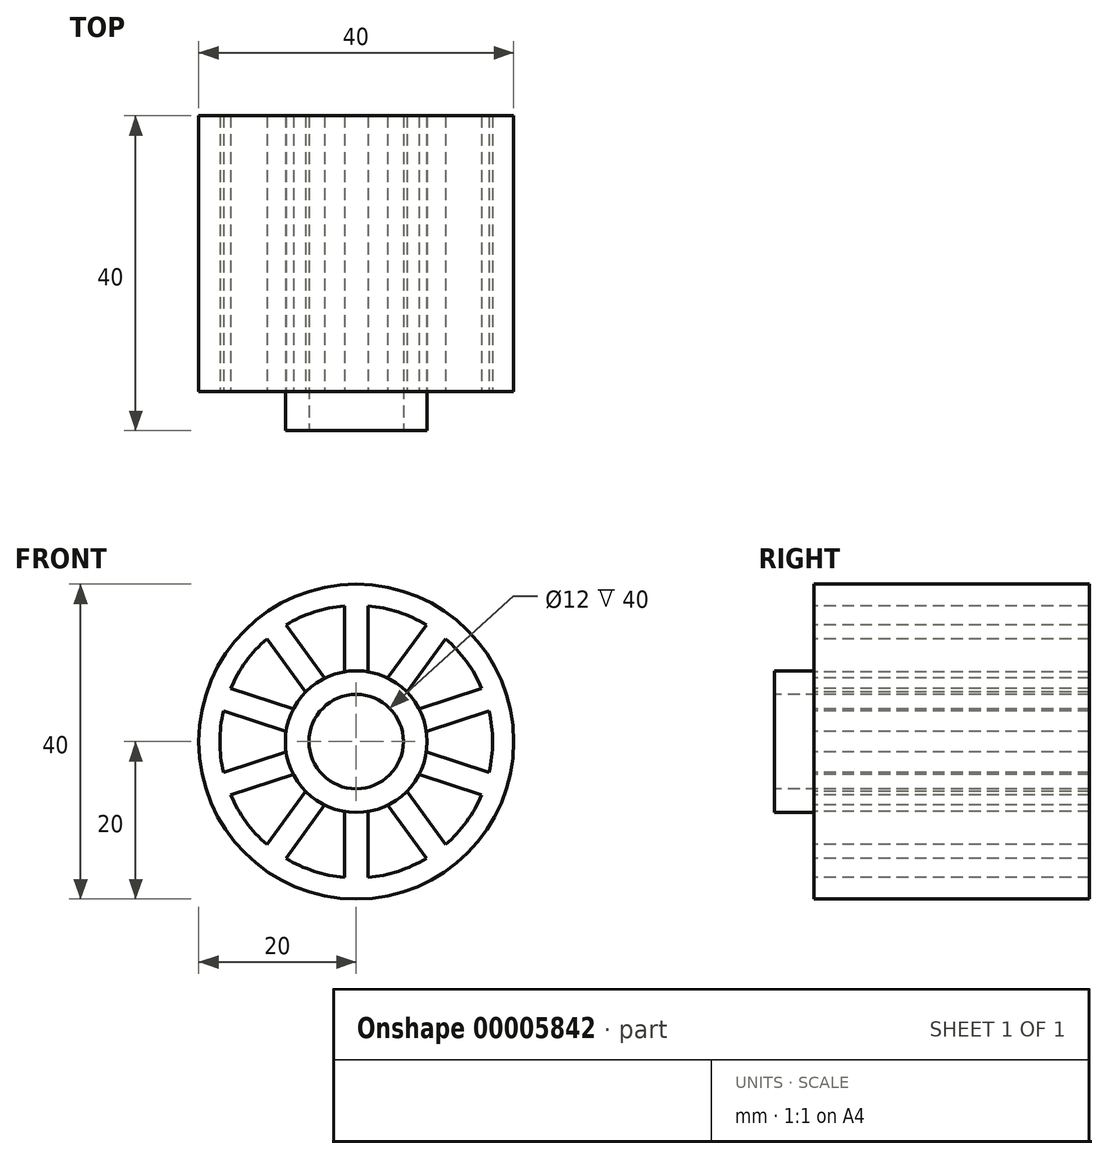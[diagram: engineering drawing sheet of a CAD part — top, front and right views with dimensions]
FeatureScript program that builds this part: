
annotation { "Feature Type Name" : "Feature", "Feature Type Description" : "" }
export const myFeature = defineFeature(function(context is Context, id is Id, definition is map)
    precondition{}
    {
        {
            var Q0;
            Q0=qCreatedBy(makeId("Front.planeOp"),FACE);
            var sketch = newSketch(context, id + "F0", { "sketchPlane" : qUnion([Q0])});
            skPoint(sketch, "E0.rect.middle", {"position": v(0, 0) * mm});
            skLineSegment(sketch, "E1.rect.left", {"start": v(1.5, 17.25) * mm, "end": v(1.5, 8.87) * mm});
            skLineSegment(sketch, "E1.rect.right", {"start": v(-1.5, 17.25) * mm, "end": v(-1.5, 8.87) * mm});
            skLineSegment(sketch, "E2.1.0", {"start": v(-16.87, 3.9) * mm, "end": v(-8.9, 1.32) * mm});
            skLineSegment(sketch, "E2.1.3", {"start": v(-15.94, 6.76) * mm, "end": v(-7.98, 4.17) * mm});
            skLineSegment(sketch, "E2.2.0", {"start": v(-8.92, -14.83) * mm, "end": v(-4, -8.06) * mm});
            skLineSegment(sketch, "E2.2.3", {"start": v(-11.35, -13.07) * mm, "end": v(-6.43, -6.3) * mm});
            skLineSegment(sketch, "E2.3.0", {"start": v(11.35, -13.07) * mm, "end": v(6.43, -6.3) * mm});
            skLineSegment(sketch, "E2.3.3", {"start": v(8.92, -14.83) * mm, "end": v(4, -8.06) * mm});
            skLineSegment(sketch, "E2.4.0", {"start": v(15.94, 6.76) * mm, "end": v(7.98, 4.17) * mm});
            skLineSegment(sketch, "E2.4.3", {"start": v(16.87, 3.9) * mm, "end": v(8.9, 1.32) * mm});
            skCircle(sketch, "E3", {"center": v(0, 0) * mm, "radius": 20 * mm});
            skArc(sketch, "E4", {"start": v(8.92, 14.83) * mm, "mid": v(5.35, 16.46) * mm, "end": v(1.5, 17.25) * mm});
            skArc(sketch, "E5", {"start": v(-7.98, -4.17) * mm, "mid": v(-7.28, -5.3) * mm, "end": v(-6.43, -6.3) * mm});
            skCircle(sketch, "E6", {"center": v(0, 0) * mm, "radius": 6 * mm});
            skPoint(sketch, "E7.orphan", {"position": v(-12.09, 14.09) * mm});
            skPoint(sketch, "E8.orphan", {"position": v(-9.66, 15.85) * mm});
            skPoint(sketch, "E9.orphan", {"position": v(12.09, 14.09) * mm});
            skArc(sketch, "E10.trimOffspring", {"start": v(15.94, 6.76) * mm, "mid": v(14, 10.18) * mm, "end": v(11.35, 13.07) * mm});
            skPoint(sketch, "E11.orphan", {"position": v(18.06, 4.3) * mm});
            skArc(sketch, "E12.trimOffspring", {"start": v(-1.5, 17.25) * mm, "mid": v(-5.35, 16.46) * mm, "end": v(-8.92, 14.83) * mm});
            skPoint(sketch, "E1.rect.bottom.end.orphan", {"position": v(-1.5, 18.5) * mm});
            skPoint(sketch, "E1.rect.bottom.start.orphan", {"position": v(1.5, 18.5) * mm});
            skLineSegment(sketch, "E13.trimOffspring", {"start": v(-4, 8.06) * mm, "end": v(-8.92, 14.83) * mm});
            skLineSegment(sketch, "E14.trimOffspring", {"start": v(-6.43, 6.3) * mm, "end": v(-11.35, 13.07) * mm});
            skArc(sketch, "E15.trimOffspring", {"start": v(-11.35, 13.07) * mm, "mid": v(-14, 10.18) * mm, "end": v(-15.94, 6.76) * mm});
            skPoint(sketch, "E16.orphan", {"position": v(-18.06, 4.3) * mm});
            skPoint(sketch, "E17.orphan", {"position": v(-17.13, 7.14) * mm});
            skArc(sketch, "E18.trimOffspring", {"start": v(-16.87, 3.9) * mm, "mid": v(-17.31, 0) * mm, "end": v(-16.87, -3.9) * mm});
            skPoint(sketch, "E19.orphan", {"position": v(-17.13, -7.14) * mm});
            skArc(sketch, "E20.trimOffspring", {"start": v(-15.94, -6.76) * mm, "mid": v(-14, -10.18) * mm, "end": v(-11.35, -13.07) * mm});
            skLineSegment(sketch, "E21.trimOffspring", {"start": v(4, 8.06) * mm, "end": v(8.92, 14.83) * mm});
            skLineSegment(sketch, "E22.trimOffspring", {"start": v(6.43, 6.3) * mm, "end": v(11.35, 13.07) * mm});
            skLineSegment(sketch, "E23.trimOffspring", {"start": v(-8.9, -1.32) * mm, "end": v(-16.87, -3.9) * mm});
            skArc(sketch, "E24.trimOffspring", {"start": v(-8.9, 1.32) * mm, "mid": v(-9, 0) * mm, "end": v(-8.9, -1.32) * mm});
            skArc(sketch, "E25.trimOffspring", {"start": v(-6.43, 6.3) * mm, "mid": v(-7.28, 5.3) * mm, "end": v(-7.98, 4.17) * mm});
            skArc(sketch, "E26.trimOffspring", {"start": v(-1.5, 8.87) * mm, "mid": v(-2.78, 8.56) * mm, "end": v(-4, 8.06) * mm});
            skArc(sketch, "E27.trimOffspring", {"start": v(4, 8.06) * mm, "mid": v(2.78, 8.56) * mm, "end": v(1.5, 8.87) * mm});
            skArc(sketch, "E28.trimOffspring", {"start": v(7.98, 4.17) * mm, "mid": v(7.28, 5.3) * mm, "end": v(6.43, 6.3) * mm});
            skArc(sketch, "E29.trimOffspring", {"start": v(8.9, -1.32) * mm, "mid": v(9, 0) * mm, "end": v(8.9, 1.32) * mm});
            skLineSegment(sketch, "E30.trimOffspring", {"start": v(8.9, -1.32) * mm, "end": v(16.87, -3.9) * mm});
            skLineSegment(sketch, "E31.trimOffspring", {"start": v(7.98, -4.17) * mm, "end": v(15.94, -6.76) * mm});
            skLineSegment(sketch, "E32.trimOffspring", {"start": v(1.5, -8.87) * mm, "end": v(1.5, -17.25) * mm});
            skLineSegment(sketch, "E33.trimOffspring", {"start": v(-1.5, -8.87) * mm, "end": v(-1.5, -17.25) * mm});
            skArc(sketch, "E34.trimOffspring", {"start": v(-4, -8.06) * mm, "mid": v(-2.78, -8.56) * mm, "end": v(-1.5, -8.87) * mm});
            skArc(sketch, "E35.trimOffspring", {"start": v(1.5, -8.87) * mm, "mid": v(2.78, -8.56) * mm, "end": v(4, -8.06) * mm});
            skPoint(sketch, "E36.orphan", {"position": v(17.13, -7.14) * mm});
            skArc(sketch, "E37.trimOffspring", {"start": v(11.35, -13.07) * mm, "mid": v(14, -10.18) * mm, "end": v(15.94, -6.76) * mm});
            skArc(sketch, "E38.trimOffspring", {"start": v(6.43, -6.3) * mm, "mid": v(7.28, -5.3) * mm, "end": v(7.98, -4.17) * mm});
            skPoint(sketch, "E39.orphan", {"position": v(9.66, -15.85) * mm});
            skPoint(sketch, "E40.orphan", {"position": v(1.5, -18.5) * mm});
            skPoint(sketch, "E41.orphan", {"position": v(-1.5, -18.5) * mm});
            skArc(sketch, "E42.trimOffspring", {"start": v(-8.92, -14.83) * mm, "mid": v(-5.35, -16.46) * mm, "end": v(-1.5, -17.25) * mm});
            skArc(sketch, "E43.trimOffspring", {"start": v(1.5, -17.25) * mm, "mid": v(5.35, -16.46) * mm, "end": v(8.92, -14.83) * mm});
            skPoint(sketch, "E44.orphan", {"position": v(-12.09, -14.09) * mm});
            skLineSegment(sketch, "E45.trimOffspring", {"start": v(-7.98, -4.17) * mm, "end": v(-15.94, -6.76) * mm});
            skArc(sketch, "E46.trimOffspring", {"start": v(16.87, -3.9) * mm, "mid": v(17.31, 0) * mm, "end": v(16.87, 3.9) * mm});
            skCircle(sketch, "E47", {"center": v(0, 0) * mm, "radius": 9 * mm});
            skSolve(sketch);
        }
        {
            var Q0;
            Q0=makeQuery(id+"F0.imprint","IMPRINT",FACE,{"disambiguationData":[TD([[makeQuery(id+"F0.imprint","IMPRINT",EDGE,{"derivedFrom":sQuery(id+"F0.wireOp",EDGE,"E1.rect.left")}),-1.0]])]});
            var Q1;
            Q1=makeQuery(id+"F0.imprint","IMPRINT",FACE,{"disambiguationData":[TD([[makeQuery(id+"F0.imprint","IMPRINT",EDGE,{"derivedFrom":sQuery(id+"F0.wireOp",EDGE,"E6")}),-1.0]])]});
            extrude(context, id + "F1", {"entities" : qUnion([Q0, Q1]), "oppositeDirection" : true, "depth" : 35 * mm});
        }
        {
            var Q0;
            Q0=makeQuery(id+"F0.imprint","IMPRINT",FACE,{"disambiguationData":[TD([[makeQuery(id+"F0.imprint","IMPRINT",EDGE,{"derivedFrom":sQuery(id+"F0.wireOp",EDGE,"E6")}),-1.0]])]});
            extrude(context, id + "F2", {"entities" : qUnion([Q0]), "operationType" : NewBodyOperationType.ADD, "depth" : 5 * mm});
        }
    });
